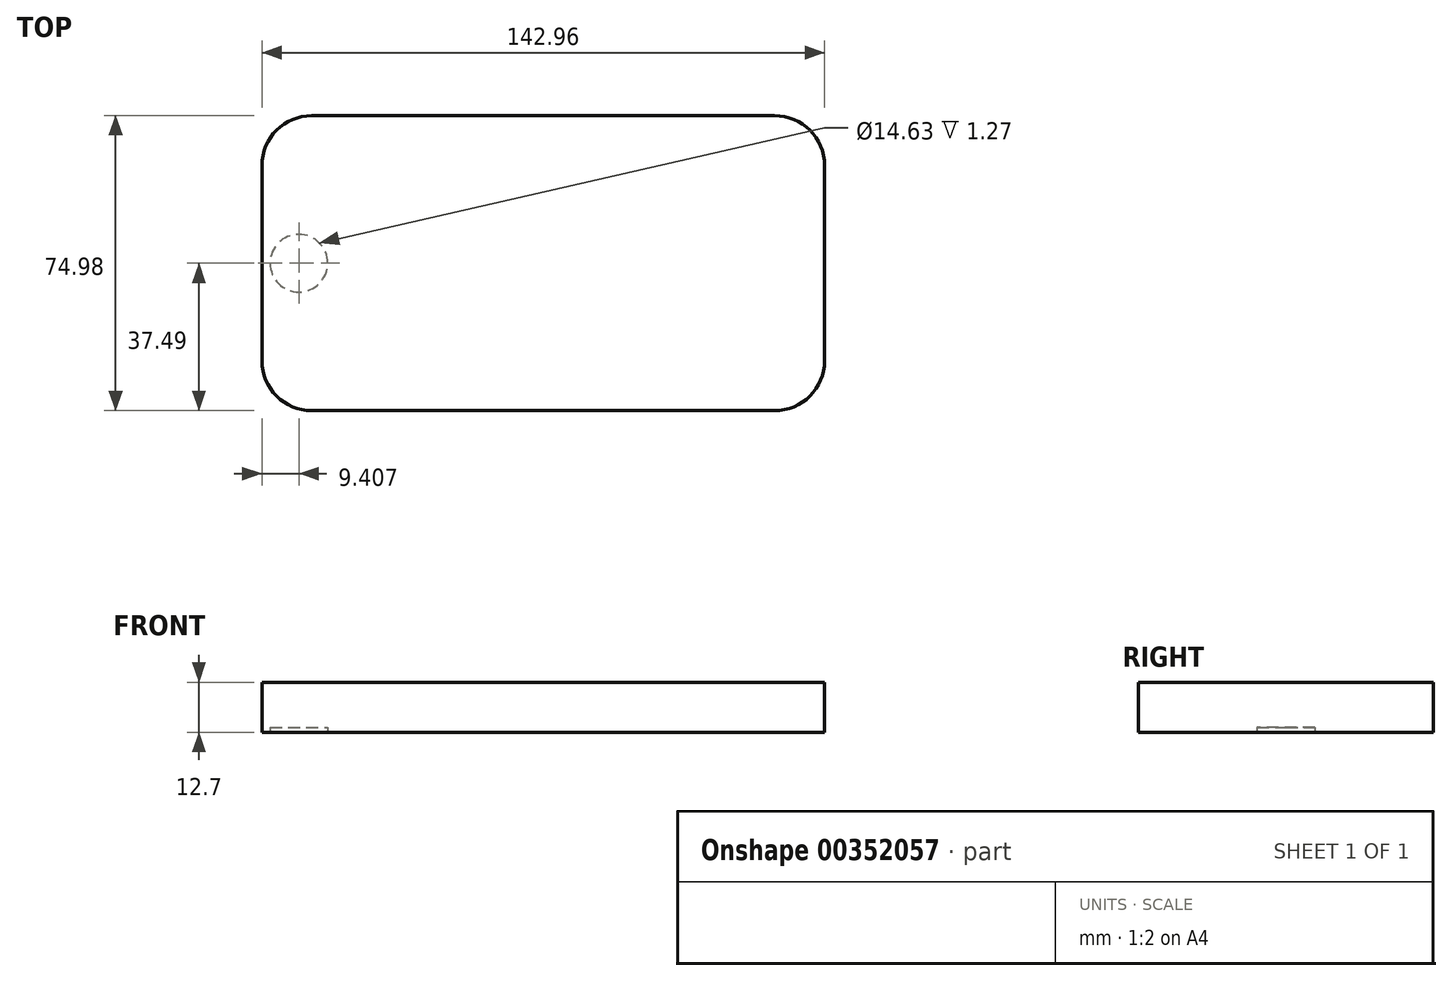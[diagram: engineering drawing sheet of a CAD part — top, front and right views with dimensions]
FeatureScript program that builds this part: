
annotation { "Feature Type Name" : "Feature", "Feature Type Description" : "" }
export const myFeature = defineFeature(function(context is Context, id is Id, definition is map)
    precondition{}
    {
        {
            var Q0;
            Q0=qCreatedBy(makeId("Top.planeOp"),FACE);
            var sketch = newSketch(context, id + "F0", { "sketchPlane" : qUnion([Q0])});
            skLineSegment(sketch, "E0.bottom", {"start": v(71.48, 37.49) * mm, "end": v(-71.48, 37.49) * mm});
            skLineSegment(sketch, "E0.top", {"start": v(71.48, -37.49) * mm, "end": v(-71.48, -37.49) * mm});
            skLineSegment(sketch, "E0.left", {"start": v(71.48, 37.49) * mm, "end": v(71.48, -37.49) * mm});
            skLineSegment(sketch, "E0.right", {"start": v(-71.48, 37.49) * mm, "end": v(-71.48, -37.49) * mm});
            skPoint(sketch, "E0.middle", {"position": v(0, 0) * mm});
            skSolve(sketch);
        }
        {
            var Q0;
            Q0=makeQuery(id+"F0.imprint","IMPRINT",FACE,{"disambiguationData":[TD([[makeQuery(id+"F0.imprint","IMPRINT",EDGE,{"derivedFrom":sQuery(id+"F0.wireOp",EDGE,"E0.bottom")}),1.0]])]});
            extrude(context, id + "F1", {"entities" : qUnion([Q0]), "depth" : 12.7 * mm});
        }
        {
            var Q0;
            Q0=makeQuery(id+"F1.opExtrude","SWEPT_EDGE",EDGE,{"disambiguationData":[OSD([sQuery(id+"F0.wireOp",EDGE,"E0.top"),sQuery(id+"F0.wireOp",EDGE,"E0.left")])]});
            var Q1;
            Q1=makeQuery(id+"F1.opExtrude","SWEPT_EDGE",EDGE,{"disambiguationData":[OSD([sQuery(id+"F0.wireOp",EDGE,"E0.bottom"),sQuery(id+"F0.wireOp",EDGE,"E0.left")])]});
            var Q2;
            Q2=makeQuery(id+"F1.opExtrude","SWEPT_EDGE",EDGE,{"disambiguationData":[OSD([sQuery(id+"F0.wireOp",EDGE,"E0.bottom"),sQuery(id+"F0.wireOp",EDGE,"E0.right")])]});
            var Q3;
            Q3=makeQuery(id+"F1.opExtrude","SWEPT_EDGE",EDGE,{"disambiguationData":[OSD([sQuery(id+"F0.wireOp",EDGE,"E0.top"),sQuery(id+"F0.wireOp",EDGE,"E0.right")])]});
            fillet(context, id + "F2", {"entities" : qUnion([Q0, Q1, Q2, Q3]), "radius" : 12.7 * mm, "tangentPropagation" : true, "allowEdgeOverflow" : false});
        }
        {
            var Q0;
            Q0=makeQuery(id+"F1.opExtrude","CAP_FACE",FACE,{"disambiguationData":[OSD([sQuery(id+"F0.wireOp",EDGE,"E0.bottom"),sQuery(id+"F0.wireOp",EDGE,"E0.top"),sQuery(id+"F0.wireOp",EDGE,"E0.left"),sQuery(id+"F0.wireOp",EDGE,"E0.right")])],"isStart":true});
            var sketch = newSketch(context, id + "F3", { "sketchPlane" : qUnion([Q0])});
            skCircle(sketch, "E1", {"center": v(-62.07, 0) * mm, "radius": 7.31 * mm});
            skSolve(sketch);
        }
        {
            var Q0;
            Q0=makeQuery(id+"F3.imprint","IMPRINT",FACE,{"disambiguationData":[TD([[makeQuery(id+"F3.imprint","IMPRINT",EDGE,{"derivedFrom":sQuery(id+"F3.wireOp",EDGE,"E1")}),1.0]])]});
            extrude(context, id + "F4", {"entities" : qUnion([Q0]), "operationType" : NewBodyOperationType.REMOVE, "oppositeDirection" : true, "depth" : 1.27 * mm});
        }
    });
